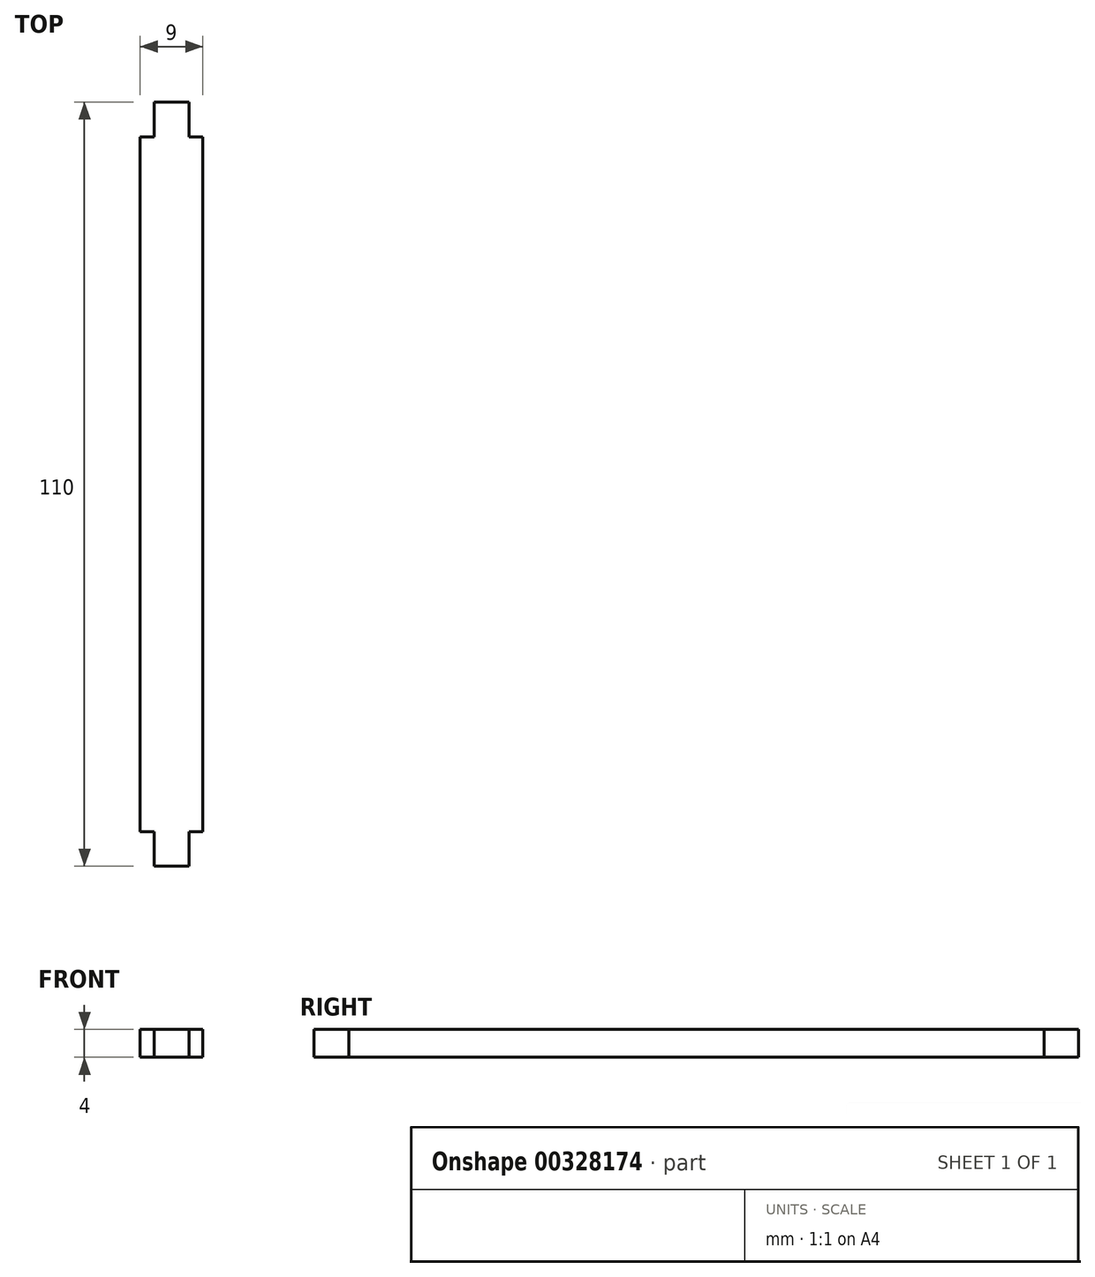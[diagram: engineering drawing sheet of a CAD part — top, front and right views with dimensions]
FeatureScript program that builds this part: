
annotation { "Feature Type Name" : "Feature", "Feature Type Description" : "" }
export const myFeature = defineFeature(function(context is Context, id is Id, definition is map)
    precondition{}
    {
        {
            var Q0;
            Q0=qCreatedBy(makeId("Top.planeOp"),FACE);
            var sketch = newSketch(context, id + "F0", { "sketchPlane" : qUnion([Q0])});
            skLineSegment(sketch, "E0", {"start": v(0, 0) * mm, "end": v(2.5, 0) * mm});
            skLineSegment(sketch, "E1", {"start": v(2.5, 0) * mm, "end": v(2.5, 5) * mm});
            skLineSegment(sketch, "E2", {"start": v(2.5, 5) * mm, "end": v(4.5, 5) * mm});
            skLineSegment(sketch, "E3", {"start": v(4.5, 5) * mm, "end": v(4.5, 105) * mm});
            skLineSegment(sketch, "E4", {"start": v(4.5, 105) * mm, "end": v(2.5, 105) * mm});
            skLineSegment(sketch, "E5", {"start": v(2.5, 105) * mm, "end": v(2.5, 110) * mm});
            skLineSegment(sketch, "E6", {"start": v(2.5, 110) * mm, "end": v(-2.5, 110) * mm});
            skLineSegment(sketch, "E7", {"start": v(-2.5, 110) * mm, "end": v(-2.5, 105) * mm});
            skLineSegment(sketch, "E8", {"start": v(-2.5, 105) * mm, "end": v(-4.5, 105) * mm});
            skLineSegment(sketch, "E9", {"start": v(-4.5, 105) * mm, "end": v(-4.5, 5) * mm});
            skLineSegment(sketch, "E10", {"start": v(-4.5, 5) * mm, "end": v(-2.5, 5) * mm});
            skLineSegment(sketch, "E11", {"start": v(-2.5, 5) * mm, "end": v(-2.5, 0) * mm});
            skLineSegment(sketch, "E12", {"start": v(-2.5, 0) * mm, "end": v(0, 0) * mm});
            skSolve(sketch);
        }
        {
            var Q0;
            Q0=makeQuery(id+"F0.imprint","IMPRINT",FACE,{"disambiguationData":[TD([[makeQuery(id+"F0.imprint","IMPRINT",EDGE,{"derivedFrom":sQuery(id+"F0.wireOp",EDGE,"E0")}),1.0]])]});
            extrude(context, id + "F1", {"entities" : qUnion([Q0]), "depth" : 4 * mm});
        }
    });
